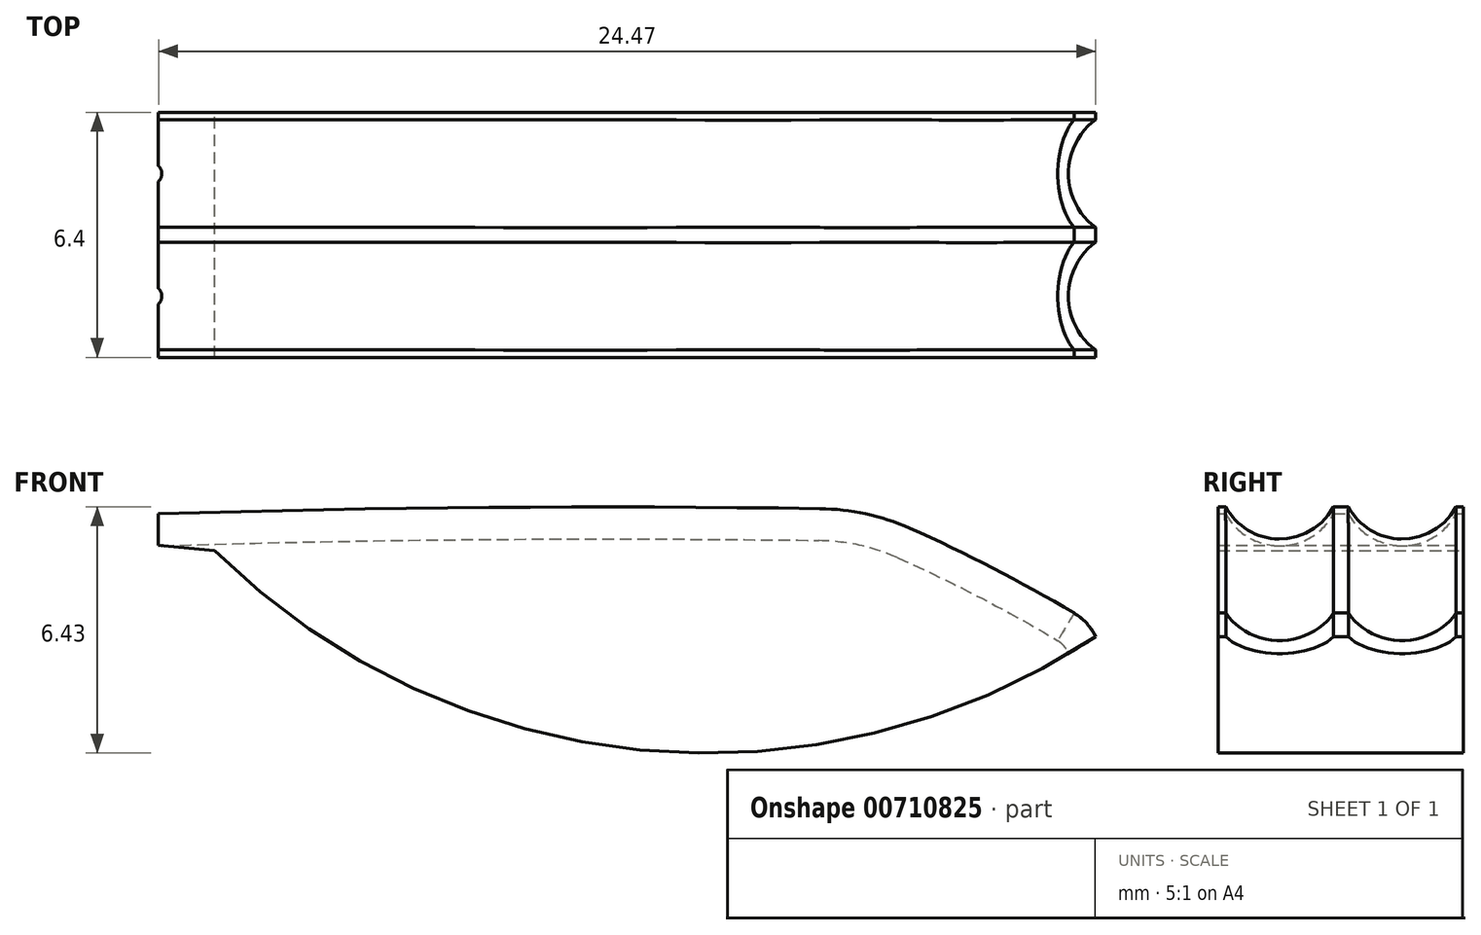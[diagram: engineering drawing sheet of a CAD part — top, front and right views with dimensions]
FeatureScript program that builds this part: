
annotation { "Feature Type Name" : "Feature", "Feature Type Description" : "" }
export const myFeature = defineFeature(function(context is Context, id is Id, definition is map)
    precondition{}
    {
        {
            var Q0;
            Q0=qCreatedBy(makeId("Front.planeOp"),FACE);
            var sketch = newSketch(context, id + "F0", { "sketchPlane" : qUnion([Q0])});
            skArc(sketch, "E0", {"start": v(-12.66, 2.24) * mm, "mid": v(-1.56, -2.96) * mm, "end": v(10.34, 0) * mm});
            skArc(sketch, "E1", {"start": v(10.34, 0) * mm, "mid": v(10.1, 0.35) * mm, "end": v(9.78, 0.61) * mm});
            skArc(sketch, "E2", {"start": v(9.78, 0.61) * mm, "mid": v(7.66, 1.79) * mm, "end": v(5.48, 2.84) * mm});
            skArc(sketch, "E3", {"start": v(5.48, 2.84) * mm, "mid": v(4.33, 3.2) * mm, "end": v(3.14, 3.34) * mm});
            skArc(sketch, "E4", {"start": v(3.14, 3.34) * mm, "mid": v(-5.5, 3.37) * mm, "end": v(-14.13, 3.2) * mm});
            skPoint(sketch, "E4.endSnap0", {"position": v(4.33, 3.2) * mm});
            skLineSegment(sketch, "E5", {"start": v(-14.13, 3.2) * mm, "end": v(-14.13, 2.38) * mm});
            skLineSegment(sketch, "E6", {"start": v(-14.13, 2.38) * mm, "end": v(-12.66, 2.24) * mm});
            skLineSegment(sketch, "E7", {"start": v(-14.13, 3.2) * mm, "end": v(-14.44, 3.2) * mm});
            skLineSegment(sketch, "E8", {"start": v(10.34, 0) * mm, "end": v(10.46, -0.25) * mm});
            skSolve(sketch);
        }
        {
            var Q0;
            Q0=makeQuery(id+"F0.imprint","IMPRINT",FACE,{"disambiguationData":[TD([[makeQuery(id+"F0.imprint","IMPRINT",EDGE,{"derivedFrom":sQuery(id+"F0.wireOp",EDGE,"E0")}),1.0]])]});
            extrude(context, id + "F1", {"entities" : qUnion([Q0]), "endBound" : BoundingType.SYMMETRIC, "depth" : 6.4 * mm, "offsetDistance" : 25 * mm});
        }
        {
            var Q0;
            Q0=qCreatedBy(makeId("Right.planeOp"),FACE);
            var sketch = newSketch(context, id + "F2", { "sketchPlane" : qUnion([Q0])});
            skCircle(sketch, "E9", {"center": v(-1.6, 4.14) * mm, "radius": 1.6 * mm});
            skCircle(sketch, "E10", {"center": v(1.6, 4.14) * mm, "radius": 1.6 * mm});
            skSolve(sketch);
        }
        {
            var Q0;
            Q0=makeQuery(id+"F2.imprint","IMPRINT",FACE,{"disambiguationData":[TD([[makeQuery(id+"F2.imprint","IMPRINT",EDGE,{"derivedFrom":sQuery(id+"F2.wireOp",EDGE,"E10")}),1.0]])]});
            var Q1;
            Q1=makeQuery(id+"F2.imprint","IMPRINT",FACE,{"disambiguationData":[TD([[makeQuery(id+"F2.imprint","IMPRINT",EDGE,{"derivedFrom":sQuery(id+"F2.wireOp",EDGE,"E9")}),1.0]])]});
            var Q2;
            Q2=sQuery(id+"F0.wireOp",EDGE,"E4");
            var Q3;
            Q3=sQuery(id+"F0.wireOp",EDGE,"E3");
            var Q4;
            Q4=sQuery(id+"F0.wireOp",EDGE,"E2");
            var Q5;
            Q5=sQuery(id+"F0.wireOp",EDGE,"E1");
            var Q6;
            Q6=sQuery(id+"F0.wireOp",EDGE,"E7");
            var Q7;
            Q7=sQuery(id+"F0.wireOp",EDGE,"E8");
            sweep(context, id + "F3", {"operationType" : NewBodyOperationType.REMOVE, "profiles" : qUnion([Q0, Q1]), "path" : qUnion([Q2, Q3, Q4, Q5, Q6, Q7])});
        }
    });
